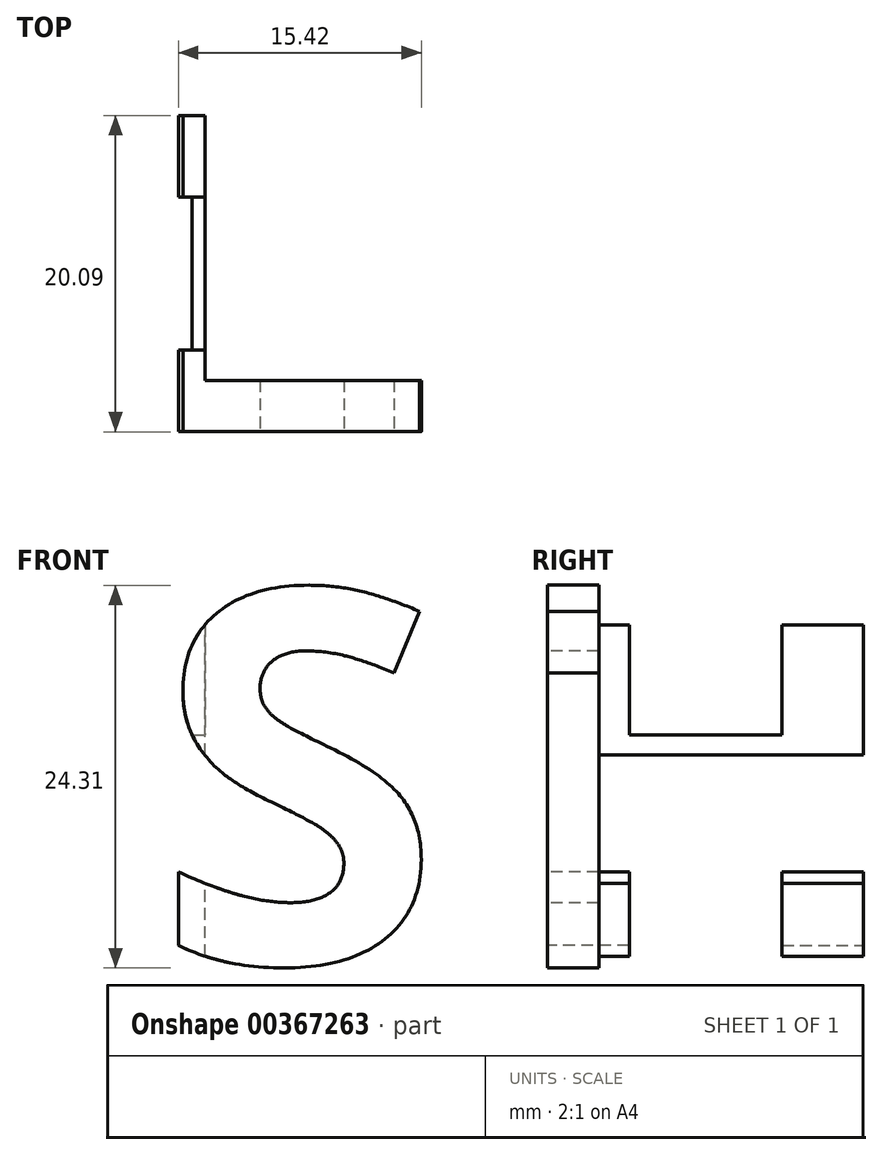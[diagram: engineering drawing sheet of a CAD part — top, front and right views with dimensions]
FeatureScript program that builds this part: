
annotation { "Feature Type Name" : "Feature", "Feature Type Description" : "" }
export const myFeature = defineFeature(function(context is Context, id is Id, definition is map)
    precondition{}
    {
        {
            var Q0;
            Q0=qCreatedBy(makeId("Front.planeOp"),FACE);
            var sketch = newSketch(context, id + "F0", { "sketchPlane" : qUnion([Q0])});
            skLineSegment(sketch, "E0.bottom", {"start": v(12.7, 12.7) * mm, "end": v(-12.7, 12.7) * mm});
            skLineSegment(sketch, "E0.top", {"start": v(12.7, -12.7) * mm, "end": v(-12.7, -12.7) * mm});
            skLineSegment(sketch, "E0.left", {"start": v(12.7, 12.7) * mm, "end": v(12.7, -12.7) * mm});
            skLineSegment(sketch, "E0.right", {"start": v(-12.7, 12.7) * mm, "end": v(-12.7, -12.7) * mm});
            skPoint(sketch, "E0.middle", {"position": v(0, 0) * mm});
            skSolve(sketch);
        }
        {
            var Q0;
            Q0 = qSketchRegion(id + "F0", true);
            extrude(context, id + "F1", {"entities" : qUnion([Q0]), "depth" : 25.4 * mm});
        }
        {
            var Q0;
            Q0=makeQuery(id+"F1.opExtrude","CAP_FACE",FACE,{"disambiguationData":[OSD([sQuery(id+"F0.wireOp",EDGE,"E0.bottom"),sQuery(id+"F0.wireOp",EDGE,"E0.top"),sQuery(id+"F0.wireOp",EDGE,"E0.left"),sQuery(id+"F0.wireOp",EDGE,"E0.right")])],"isStart":false});
            var sketch = newSketch(context, id + "F2", { "sketchPlane" : qUnion([Q0])});
            skText(sketch, "E1", { "text": "S", "fontName": "OpenSans-Bold.ttf"});
            const initialGuessF2  = {"E1": [-0.00954, -0.01193, 1, 0, 0.02385]};
            skSetInitialGuess(sketch, initialGuessF2);
            skSolve(sketch);
        }
        {
            var Q0;
            Q0=makeQuery(id+"F1.opExtrude","SWEPT_FACE",FACE,{"disambiguationData":[OSD([sQuery(id+"F0.wireOp",EDGE,"E0.bottom")])]});
            var sketch = newSketch(context, id + "F3", { "sketchPlane" : qUnion([Q0])});
            skLineSegment(sketch, "E2", {"start": v(-12.7, -12.7) * mm, "end": v(12.7, -12.7) * mm, "construction": true});
            skPoint(sketch, "E3", {"position": v(0, -12.7) * mm});
            skLineSegment(sketch, "E4.bottom", {"start": v(-12.7, 0) * mm, "end": v(-6.35, 0) * mm});
            skLineSegment(sketch, "E4.top", {"start": v(-12.7, -25.4) * mm, "end": v(-6.35, -25.4) * mm});
            skLineSegment(sketch, "E4.left", {"start": v(-12.7, 0) * mm, "end": v(-12.7, -25.4) * mm});
            skLineSegment(sketch, "E4.right", {"start": v(-6.35, 0) * mm, "end": v(-6.35, -25.4) * mm});
            skLineSegment(sketch, "E5.bottom", {"start": v(-12.7, -25.4) * mm, "end": v(12.7, -25.4) * mm});
            skLineSegment(sketch, "E5.top", {"start": v(-12.7, -19.05) * mm, "end": v(12.7, -19.05) * mm});
            skLineSegment(sketch, "E5.left", {"start": v(-12.7, -25.4) * mm, "end": v(-12.7, -19.05) * mm});
            skLineSegment(sketch, "E5.right", {"start": v(12.7, -25.4) * mm, "end": v(12.7, -19.05) * mm});
            skSolve(sketch);
        }
        {
            var Q0;
            Q0=makeQuery(id+"F1.opExtrude","SWEPT_FACE",FACE,{"disambiguationData":[OSD([sQuery(id+"F0.wireOp",EDGE,"E0.left")])]});
            var sketch = newSketch(context, id + "F4", { "sketchPlane" : qUnion([Q0])});
            skText(sketch, "E6", { "text": "H", "fontName": "OpenSans-Bold.ttf"});
            skLineSegment(sketch, "E7", {"start": v(-25.4, 0) * mm, "end": v(0, 0) * mm, "construction": true});
            skPoint(sketch, "E8", {"position": v(-12.7, 0) * mm});
            const initialGuessF4  = {"E6": [-0.0254, -0.01236, 1, 0, 0.02472]};
            skSetInitialGuess(sketch, initialGuessF4);
            skSolve(sketch);
        }
        {
            var Q0;
            Q0=makeQuery(id+"F2.imprint","IMPRINT",FACE,{"disambiguationData":[TD([[makeQuery(id+"F2.imprint","IMPRINT",EDGE,{"derivedFrom":sQuery(id+"F2.wireOp",EDGE,"E1.sketch_text.stroke-0")}),1.0]])]});
            extrude(context, id + "F5", {"entities" : qUnion([Q0]), "operationType" : NewBodyOperationType.REMOVE, "endBound" : BoundingType.THROUGH_ALL, "oppositeDirection" : true, "depth" : 25.4 * mm});
        }
        {
            var Q0;
            {var subQ0=sQuery(id+"F3.wireOp",EDGE,"E4.right");var subQ4=sQuery(id+"F3.wireOp",EDGE,"E5.top");var subQ5=makeQuery(id+"F3.imprint","INTERSECT",VERTEX,{"derivedFrom":[subQ0,subQ4]});Q0=makeQuery(id+"F3.imprint","IMPRINT",FACE,{"disambiguationData":[TD([[makeQuery(id+"F3.imprint","IMPRINT",EDGE,{"disambiguationData":[TD([[subQ5,1.0]])],"derivedFrom":subQ0}),1.0]])]});}
            extrude(context, id + "F6", {"entities" : qUnion([Q0]), "operationType" : NewBodyOperationType.REMOVE, "endBound" : BoundingType.THROUGH_ALL, "oppositeDirection" : true, "depth" : 25.4 * mm});
        }
        {
            var Q0;
            Q0=makeQuery(id+"F4.imprint","IMPRINT",FACE,{"disambiguationData":[TD([[makeQuery(id+"F4.imprint","IMPRINT",EDGE,{"derivedFrom":sQuery(id+"F4.wireOp",EDGE,"E6.sketch_text.stroke-0")}),1.0]])]});
            extrude(context, id + "F7", {"entities" : qUnion([Q0]), "operationType" : NewBodyOperationType.REMOVE, "endBound" : BoundingType.THROUGH_ALL, "oppositeDirection" : true, "depth" : 25.4 * mm});
        }
    });
